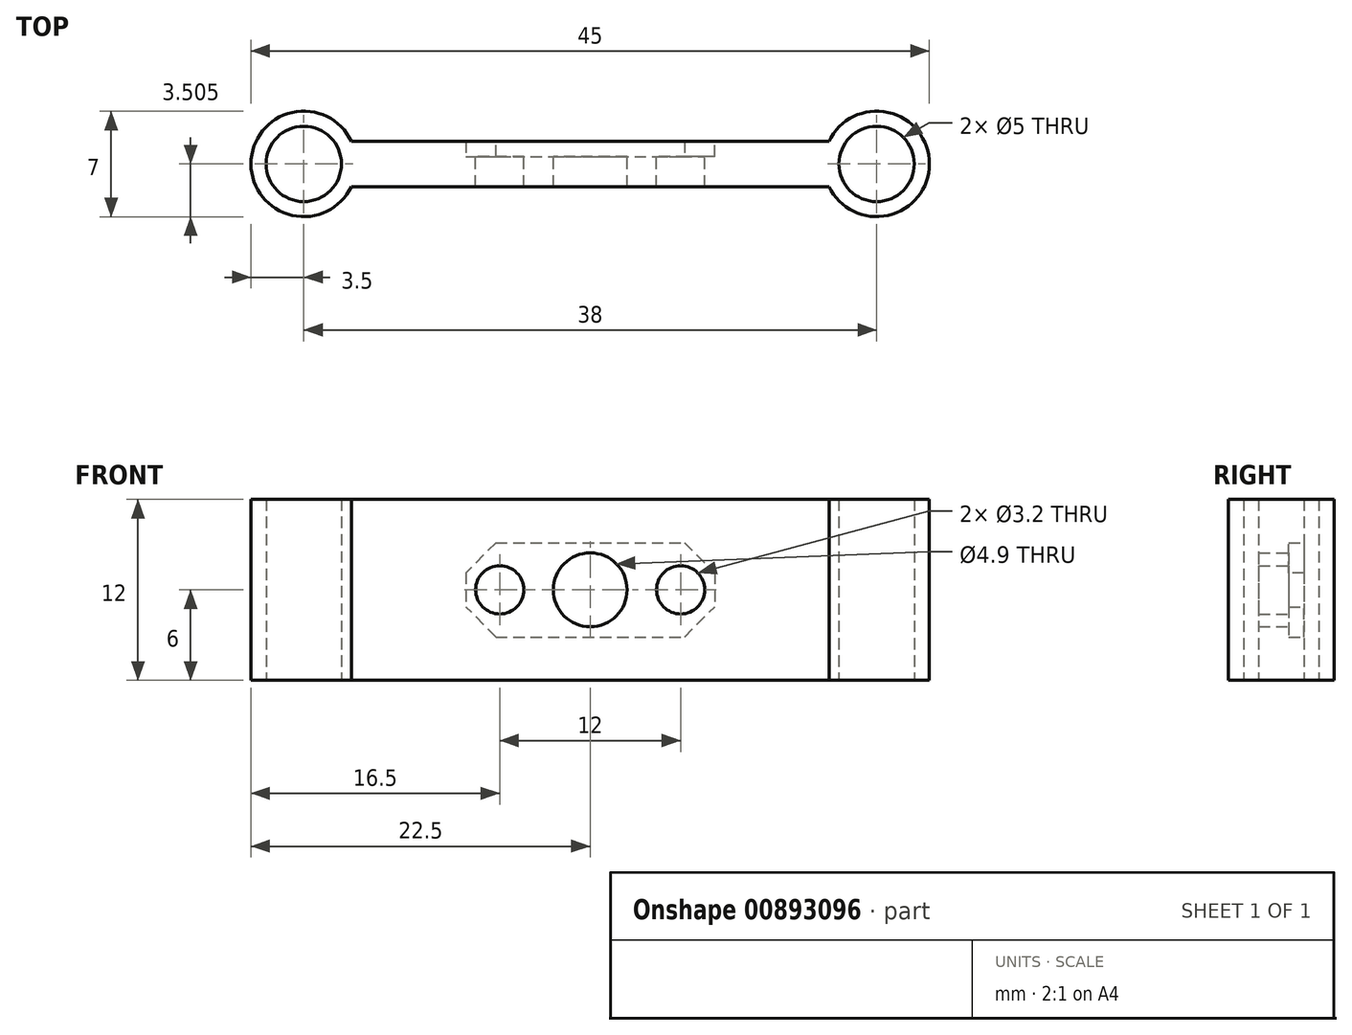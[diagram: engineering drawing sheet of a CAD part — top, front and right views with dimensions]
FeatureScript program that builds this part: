
annotation { "Feature Type Name" : "Feature", "Feature Type Description" : "" }
export const myFeature = defineFeature(function(context is Context, id is Id, definition is map)
    precondition{}
    {
        {
            var Q0;
            Q0=qCreatedBy(makeId("Top.planeOp"),FACE);
            var sketch = newSketch(context, id + "F0", { "sketchPlane" : qUnion([Q0])});
            skLineSegment(sketch, "E0.bottom", {"start": v(-19, 1.12) * mm, "end": v(19, 1.12) * mm});
            skLineSegment(sketch, "E0.top", {"start": v(-19, -1.88) * mm, "end": v(19, -1.88) * mm});
            skLineSegment(sketch, "E0.left", {"start": v(-19, 1.12) * mm, "end": v(-19, -1.88) * mm});
            skLineSegment(sketch, "E0.right", {"start": v(19, 1.12) * mm, "end": v(19, -1.88) * mm});
            skPoint(sketch, "E1", {"position": v(-19, -0.38) * mm});
            skCircle(sketch, "E2", {"center": v(-19, -0.38) * mm, "radius": 3.5 * mm});
            skCircle(sketch, "E3", {"center": v(19, -0.38) * mm, "radius": 3.5 * mm});
            skSolve(sketch);
        }
        {
            var Q0;
            Q0=qSketchRegion(id+"F0",true);
            extrude(context, id + "F1", {"entities" : qUnion([Q0]), "depth" : 12 * mm, "offsetDistance" : 25 * mm});
        }
        {
            var Q0;
            Q0=sQuery(id+"F0.wireOp",VERTEX,"35dba5de-8aa0-4c4d-8b60-120a7edc57c8");
            var Q1;
            Q1=sQuery(id+"F0.wireOp",VERTEX,"E3.center");
            var Q2;
            Q2=makeQuery(id+"F1.opExtrude","SWEPT_BODY",BODY,{"disambiguationData":[OSD([sQuery(id+"F0.wireOp",EDGE,"E0.bottom"),sQuery(id+"F0.wireOp",EDGE,"E0.top"),sQuery(id+"F0.wireOp",EDGE,"E2"),sQuery(id+"F0.wireOp",EDGE,"E3")])]});
            hole(context, id + "F2", {"style" : HoleStyle.SIMPLE, "endStyle" : HoleEndStyle.BLIND, "oppositeDirection" : true, "holeDiameter" : 5 * mm, "majorDiameter" : 5 * mm, "holeDepth" : 15 * mm, "isTappedThrough" : true, "tappedDepth" : 12 * mm, "tapClearance" : 3, "locations" : qUnion([Q0, Q1]), "scope" : qUnion([Q2])});
        }
        {
            var Q0;
            Q0=sQuery(id+"F0.wireOp",VERTEX,"E1");
            var Q1;
            Q1=makeQuery(id+"F1.opExtrude","SWEPT_BODY",BODY,{"disambiguationData":[OSD([sQuery(id+"F0.wireOp",EDGE,"E0.bottom"),sQuery(id+"F0.wireOp",EDGE,"E0.top"),sQuery(id+"F0.wireOp",EDGE,"E2"),sQuery(id+"F0.wireOp",EDGE,"E3")])]});
            hole(context, id + "F3", {"style" : HoleStyle.SIMPLE, "endStyle" : HoleEndStyle.BLIND, "oppositeDirection" : true, "holeDiameter" : 5 * mm, "majorDiameter" : 5 * mm, "holeDepth" : 15 * mm, "isTappedThrough" : true, "tappedDepth" : 12 * mm, "tapClearance" : 3, "locations" : qUnion([Q0]), "scope" : qUnion([Q1])});
        }
        {
            var Q0;
            Q0=makeQuery(id+"F1.opExtrude","SWEPT_FACE",FACE,{"disambiguationData":[OSD([sQuery(id+"F0.wireOp",EDGE,"E0.bottom")])]});
            var sketch = newSketch(context, id + "F4", { "sketchPlane" : qUnion([Q0])});
            skPoint(sketch, "E4", {"position": v(0, 6) * mm});
            skPoint(sketch, "E4.positionSnap0", {"position": v(0, 12) * mm});
            skPoint(sketch, "E5", {"position": v(-6, 6) * mm});
            skPoint(sketch, "E6", {"position": v(6, 6) * mm});
            skSolve(sketch);
        }
        {
            var Q0;
            Q0=sQuery(id+"F4.wireOp",VERTEX,"E4");
            var Q1;
            Q1=makeQuery(id+"F1.opExtrude","SWEPT_BODY",BODY,{"disambiguationData":[OSD([sQuery(id+"F0.wireOp",EDGE,"E0.bottom"),sQuery(id+"F0.wireOp",EDGE,"E0.top"),sQuery(id+"F0.wireOp",EDGE,"E2"),sQuery(id+"F0.wireOp",EDGE,"E3")])]});
            hole(context, id + "F5", {"style" : HoleStyle.SIMPLE, "endStyle" : HoleEndStyle.BLIND, "holeDiameter" : 4.9 * mm, "majorDiameter" : 5 * mm, "holeDepth" : 10 * mm, "isTappedThrough" : true, "tappedDepth" : 12 * mm, "tapClearance" : 3, "locations" : qUnion([Q0]), "scope" : qUnion([Q1])});
        }
        {
            var Q0;
            Q0=sQuery(id+"F4.wireOp",VERTEX,"E5");
            var Q1;
            Q1=makeQuery(id+"F1.opExtrude","SWEPT_BODY",BODY,{"disambiguationData":[OSD([sQuery(id+"F0.wireOp",EDGE,"E0.bottom"),sQuery(id+"F0.wireOp",EDGE,"E0.top"),sQuery(id+"F0.wireOp",EDGE,"E2"),sQuery(id+"F0.wireOp",EDGE,"E3")])]});
            hole(context, id + "F6", {"style" : HoleStyle.SIMPLE, "endStyle" : HoleEndStyle.BLIND, "holeDiameter" : 3.2 * mm, "majorDiameter" : 5 * mm, "holeDepth" : 15 * mm, "isTappedThrough" : true, "tappedDepth" : 12 * mm, "tapClearance" : 3, "locations" : qUnion([Q0]), "scope" : qUnion([Q1])});
        }
        {
            var Q0;
            Q0=sQuery(id+"F4.wireOp",VERTEX,"E6");
            var Q1;
            Q1=makeQuery(id+"F1.opExtrude","SWEPT_BODY",BODY,{"disambiguationData":[OSD([sQuery(id+"F0.wireOp",EDGE,"E0.bottom"),sQuery(id+"F0.wireOp",EDGE,"E0.top"),sQuery(id+"F0.wireOp",EDGE,"E2"),sQuery(id+"F0.wireOp",EDGE,"E3")])]});
            hole(context, id + "F7", {"style" : HoleStyle.SIMPLE, "endStyle" : HoleEndStyle.BLIND, "holeDiameter" : 3.2 * mm, "majorDiameter" : 5 * mm, "holeDepth" : 15 * mm, "isTappedThrough" : true, "tappedDepth" : 12 * mm, "tapClearance" : 3, "locations" : qUnion([Q0]), "scope" : qUnion([Q1])});
        }
        {
            var Q0;
            Q0=makeQuery(id+"F1.opExtrude","SWEPT_FACE",FACE,{"disambiguationData":[OSD([sQuery(id+"F0.wireOp",EDGE,"E0.bottom")])]});
            var sketch = newSketch(context, id + "F8", { "sketchPlane" : qUnion([Q0])});
            skPoint(sketch, "E7", {"position": v(0, 6) * mm});
            skLineSegment(sketch, "E8.bottom", {"start": v(8.25, 9.13) * mm, "end": v(-8.25, 9.12) * mm});
            skLineSegment(sketch, "E8.top", {"start": v(8.25, 2.88) * mm, "end": v(-8.25, 2.87) * mm});
            skLineSegment(sketch, "E8.left", {"start": v(8.25, 9.13) * mm, "end": v(8.25, 2.88) * mm});
            skLineSegment(sketch, "E8.right", {"start": v(-8.25, 9.12) * mm, "end": v(-8.25, 2.88) * mm});
            skSolve(sketch);
        }
        {
            var Q0;
            Q0 = qSketchRegion(id + "F8", true);
            extrude(context, id + "F9", {"entities" : qUnion([Q0]), "operationType" : NewBodyOperationType.REMOVE, "oppositeDirection" : true, "depth" : 1 * mm, "offsetDistance" : 25 * mm});
        }
        {
            var Q0;
            Q0=makeQuery(id+"F9.boolean.opBoolean","COPY",EDGE,{"derivedFrom":makeQuery(id+"F9.opExtrude","SWEPT_EDGE",EDGE,{"disambiguationData":[OSD([sQuery(id+"F8.wireOp",EDGE,"E8.bottom"),sQuery(id+"F8.wireOp",EDGE,"E8.right")])]})});
            var Q1;
            Q1=makeQuery(id+"F9.boolean.opBoolean","COPY",EDGE,{"derivedFrom":makeQuery(id+"F9.opExtrude","SWEPT_EDGE",EDGE,{"disambiguationData":[OSD([sQuery(id+"F8.wireOp",EDGE,"E8.top"),sQuery(id+"F8.wireOp",EDGE,"E8.right")])]})});
            var Q2;
            Q2=makeQuery(id+"F9.boolean.opBoolean","COPY",EDGE,{"derivedFrom":makeQuery(id+"F9.opExtrude","SWEPT_EDGE",EDGE,{"disambiguationData":[OSD([sQuery(id+"F8.wireOp",EDGE,"E8.bottom"),sQuery(id+"F8.wireOp",EDGE,"E8.left")])]})});
            var Q3;
            Q3=makeQuery(id+"F9.boolean.opBoolean","COPY",EDGE,{"derivedFrom":makeQuery(id+"F9.opExtrude","SWEPT_EDGE",EDGE,{"disambiguationData":[OSD([sQuery(id+"F8.wireOp",EDGE,"E8.top"),sQuery(id+"F8.wireOp",EDGE,"E8.left")])]})});
            chamfer(context, id + "F10", {"entities" : qUnion([Q0, Q1, Q2, Q3]), "width" : 2 * mm});
        }
    });
